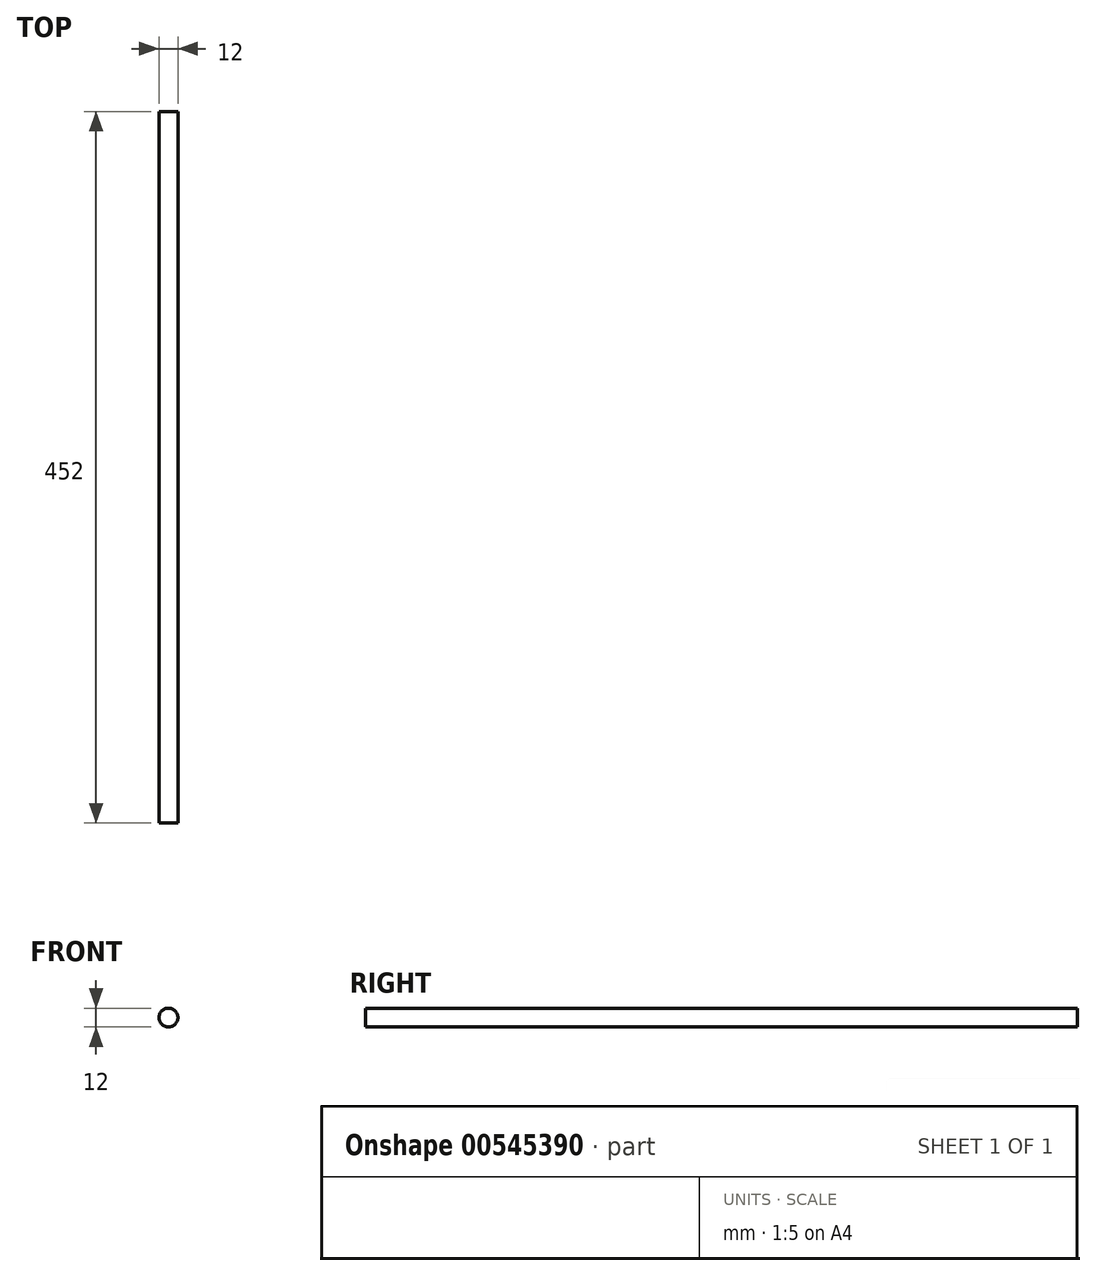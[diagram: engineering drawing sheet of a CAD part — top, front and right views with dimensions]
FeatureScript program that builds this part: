
annotation { "Feature Type Name" : "Feature", "Feature Type Description" : "" }
export const myFeature = defineFeature(function(context is Context, id is Id, definition is map)
    precondition{}
    {
        {
            var Q0;
            Q0=qCreatedBy(makeId("Front.planeOp"),FACE);
            var sketch = newSketch(context, id + "F0", { "sketchPlane" : qUnion([Q0])});
            skCircle(sketch, "E0", {"center": v(0, 0) * mm, "radius": 6 * mm});
            skSolve(sketch);
        }
        {
            var Q0;
            Q0 = qSketchRegion(id + "F0", true);
            extrude(context, id + "F1", {"entities" : qUnion([Q0]), "depth" : 452 * mm, "offsetDistance" : 25.4 * mm});
        }
    });
